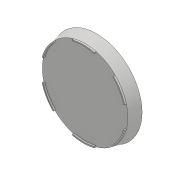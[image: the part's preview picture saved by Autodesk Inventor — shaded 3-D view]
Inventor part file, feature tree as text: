
AUTODESK INVENTOR PART (.ipt)
format: ipt  version: 2017 (Build 210142000, 142)  size: 143,872 bytes
history: native  units: mm
features: sketch x2, revolve x1, shell x1, fillet x1, extrude x1, pattern_circular x1, projected_geometry x1
ambient origin geometry x8: Origin, YZ Plane, XZ Plane, XY Plane, X Axis, Y Axis, Z Axis, Center Point
bodies: Solid1 (feature_tree)
feature tree (8):
  revolve  "Revolution1"  [1 undecoded]
  shell  "Shell1"  Thickness=10.0mm
  fillet  "Fillet1"  [1 undecoded]
  extrude  "Extrusion1"  Depth=1.0mm
  pattern_circular  "Circular Pattern1"  [2 undecoded]
  sketch  "Sketch1"  dims[d0=13.439035mm d2=37.0mm d3=10.0mm d4=90.0deg]
  sketch  "Sketch2"  dims[d5=1.2mm d6=1.0mm d8=72.0mm d9=15.0deg d10=15.0deg d11=1.5mm d12=0.0mm d13=60.0mm d14=360.0deg]
  projected_geometry  "Projected Loop1"
note: 4 required parameter values undecoded (feature->parameter linkage not recoverable at this tier; creation-order binding heuristic only, values carry confidence <= 0.55)